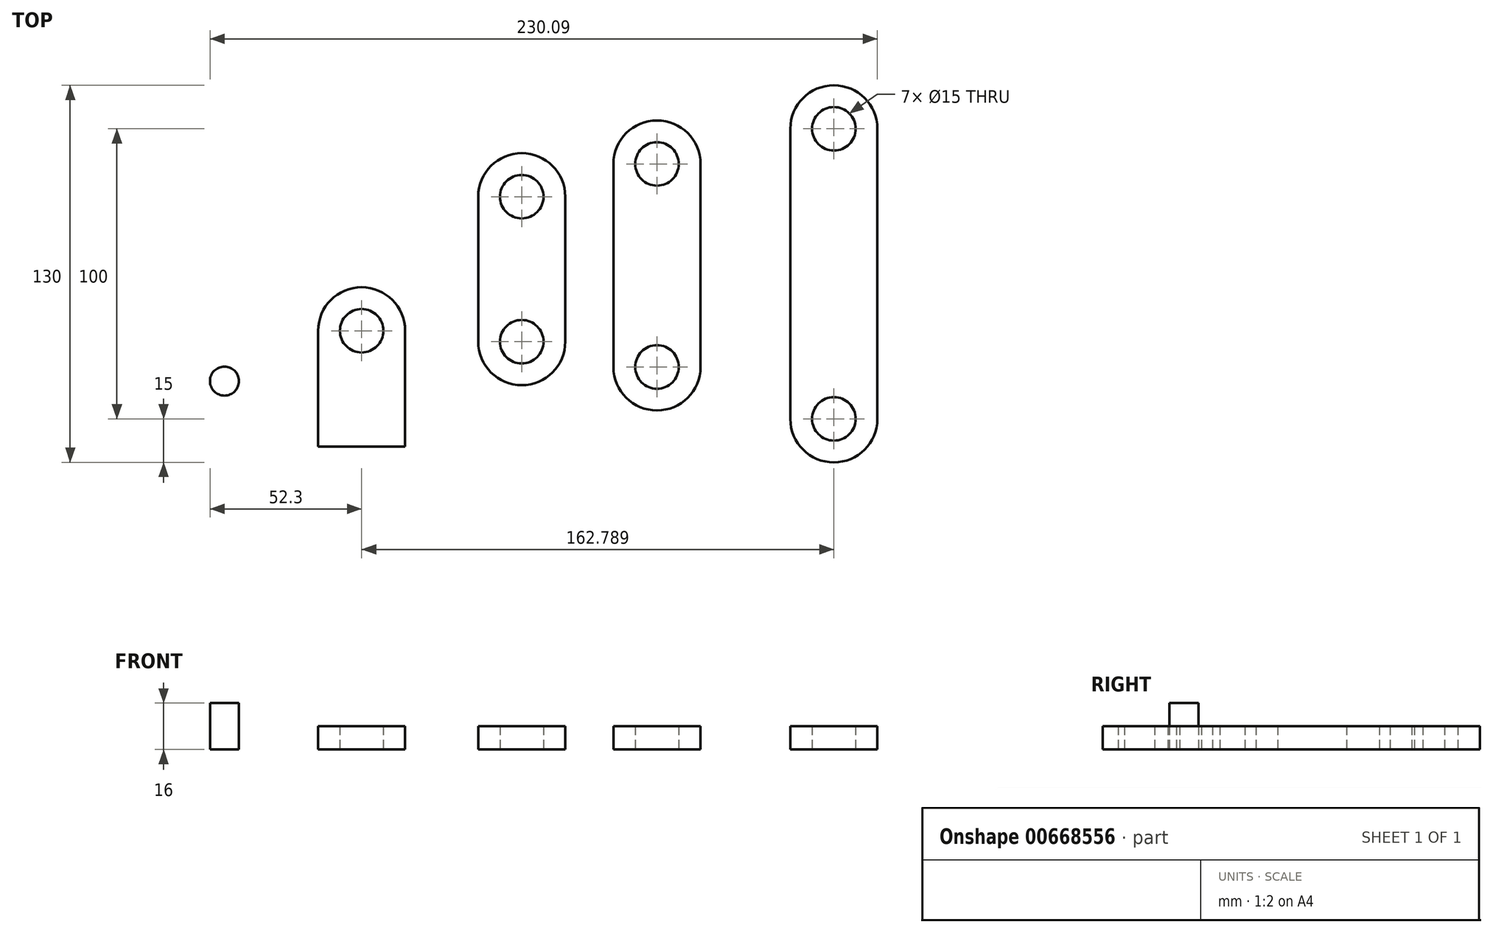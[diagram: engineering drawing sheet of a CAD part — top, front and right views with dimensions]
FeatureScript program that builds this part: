
annotation { "Feature Type Name" : "Feature", "Feature Type Description" : "" }
export const myFeature = defineFeature(function(context is Context, id is Id, definition is map)
    precondition{}
    {
        {
            var Q0;
            Q0=qCreatedBy(makeId("Top.planeOp"),FACE);
            var sketch = newSketch(context, id + "F0", { "sketchPlane" : qUnion([Q0])});
            skArc(sketch, "E0", {"start": v(15, 40) * mm, "mid": v(0, 55) * mm, "end": v(-15, 40) * mm});
            skLineSegment(sketch, "E1", {"start": v(-15, 40) * mm, "end": v(-15, 0) * mm});
            skLineSegment(sketch, "E2", {"start": v(-15, 0) * mm, "end": v(15, 0) * mm});
            skLineSegment(sketch, "E3", {"start": v(15, 0) * mm, "end": v(15, 40) * mm});
            skCircle(sketch, "E4", {"center": v(0, 40) * mm, "radius": 7.5 * mm});
            skSolve(sketch);
        }
        {
            var Q0;
            Q0=makeQuery(id+"F0.imprint","IMPRINT",FACE,{"disambiguationData":[TD([[makeQuery(id+"F0.imprint","IMPRINT",EDGE,{"derivedFrom":sQuery(id+"F0.wireOp",EDGE,"E0")}),1.0]])]});
            extrude(context, id + "F1", {"entities" : qUnion([Q0]), "depth" : 8 * mm, "offsetDistance" : 25 * mm});
        }
        {
            var Q0;
            Q0=qCreatedBy(makeId("Top.planeOp"),FACE);
            var sketch = newSketch(context, id + "F2", { "sketchPlane" : qUnion([Q0])});
            skArc(sketch, "E5", {"start": v(70.18, 86.22) * mm, "mid": v(55.18, 101.22) * mm, "end": v(40.18, 86.22) * mm});
            skArc(sketch, "E6", {"start": v(40.18, 36.22) * mm, "mid": v(55.18, 21.22) * mm, "end": v(70.18, 36.22) * mm});
            skLineSegment(sketch, "E7", {"start": v(40.18, 86.22) * mm, "end": v(40.18, 36.22) * mm});
            skLineSegment(sketch, "E8", {"start": v(70.18, 86.22) * mm, "end": v(70.18, 36.22) * mm});
            skCircle(sketch, "E9", {"center": v(55.18, 86.22) * mm, "radius": 7.5 * mm});
            skCircle(sketch, "E10", {"center": v(55.18, 36.22) * mm, "radius": 7.5 * mm});
            skSolve(sketch);
        }
        {
            var Q0;
            Q0=makeQuery(id+"F2.imprint","IMPRINT",FACE,{"disambiguationData":[TD([[makeQuery(id+"F2.imprint","IMPRINT",EDGE,{"derivedFrom":sQuery(id+"F2.wireOp",EDGE,"E5")}),1.0]])]});
            extrude(context, id + "F3", {"entities" : qUnion([Q0]), "depth" : 8 * mm, "offsetDistance" : 25 * mm});
        }
        {
            var Q0;
            Q0=qCreatedBy(makeId("Top.planeOp"),FACE);
            var sketch = newSketch(context, id + "F4", { "sketchPlane" : qUnion([Q0])});
            skArc(sketch, "E11", {"start": v(86.81, 27.52) * mm, "mid": v(101.81, 12.52) * mm, "end": v(116.81, 27.52) * mm});
            skArc(sketch, "E12", {"start": v(116.81, 97.52) * mm, "mid": v(101.81, 112.52) * mm, "end": v(86.81, 97.52) * mm});
            skLineSegment(sketch, "E13", {"start": v(86.81, 97.52) * mm, "end": v(86.81, 27.52) * mm});
            skLineSegment(sketch, "E14", {"start": v(116.81, 97.52) * mm, "end": v(116.81, 27.52) * mm});
            skCircle(sketch, "E15", {"center": v(101.81, 97.52) * mm, "radius": 7.5 * mm});
            skCircle(sketch, "E16", {"center": v(101.81, 27.52) * mm, "radius": 7.5 * mm});
            skSolve(sketch);
        }
        {
            var Q0;
            Q0=qSketchRegion(id+"F4",true);
            extrude(context, id + "F5", {"entities" : qUnion([Q0]), "depth" : 8 * mm, "offsetDistance" : 25 * mm});
        }
        {
            var Q0;
            Q0=qCreatedBy(makeId("Top.planeOp"),FACE);
            var sketch = newSketch(context, id + "F6", { "sketchPlane" : qUnion([Q0])});
            skArc(sketch, "E17", {"start": v(177.79, 109.62) * mm, "mid": v(162.79, 124.62) * mm, "end": v(147.79, 109.62) * mm});
            skArc(sketch, "E18", {"start": v(147.79, 9.62) * mm, "mid": v(162.79, -5.38) * mm, "end": v(177.79, 9.62) * mm});
            skLineSegment(sketch, "E19", {"start": v(147.79, 109.62) * mm, "end": v(147.79, 9.62) * mm});
            skLineSegment(sketch, "E20", {"start": v(177.79, 109.62) * mm, "end": v(177.79, 9.62) * mm});
            skCircle(sketch, "E21", {"center": v(162.79, 109.62) * mm, "radius": 7.5 * mm});
            skCircle(sketch, "E22", {"center": v(162.79, 9.62) * mm, "radius": 7.5 * mm});
            skSolve(sketch);
        }
        {
            var Q0;
            Q0=makeQuery(id+"F6.imprint","IMPRINT",FACE,{"disambiguationData":[TD([[makeQuery(id+"F6.imprint","IMPRINT",EDGE,{"derivedFrom":sQuery(id+"F6.wireOp",EDGE,"E17")}),1.0]])]});
            extrude(context, id + "F7", {"entities" : qUnion([Q0]), "depth" : 8 * mm, "offsetDistance" : 25 * mm});
        }
        {
            var Q0;
            Q0=qCreatedBy(makeId("Top.planeOp"),FACE);
            var sketch = newSketch(context, id + "F8", { "sketchPlane" : qUnion([Q0])});
            skCircle(sketch, "E23", {"center": v(-47.3, 22.64) * mm, "radius": 5 * mm});
            skSolve(sketch);
        }
        {
            var Q0;
            Q0=makeQuery(id+"F8.imprint","IMPRINT",FACE,{"disambiguationData":[TD([[makeQuery(id+"F8.imprint","IMPRINT",EDGE,{"derivedFrom":sQuery(id+"F8.wireOp",EDGE,"E23")}),1.0]])]});
            extrude(context, id + "F9", {"entities" : qUnion([Q0]), "depth" : 16 * mm, "offsetDistance" : 25 * mm});
        }
    });
